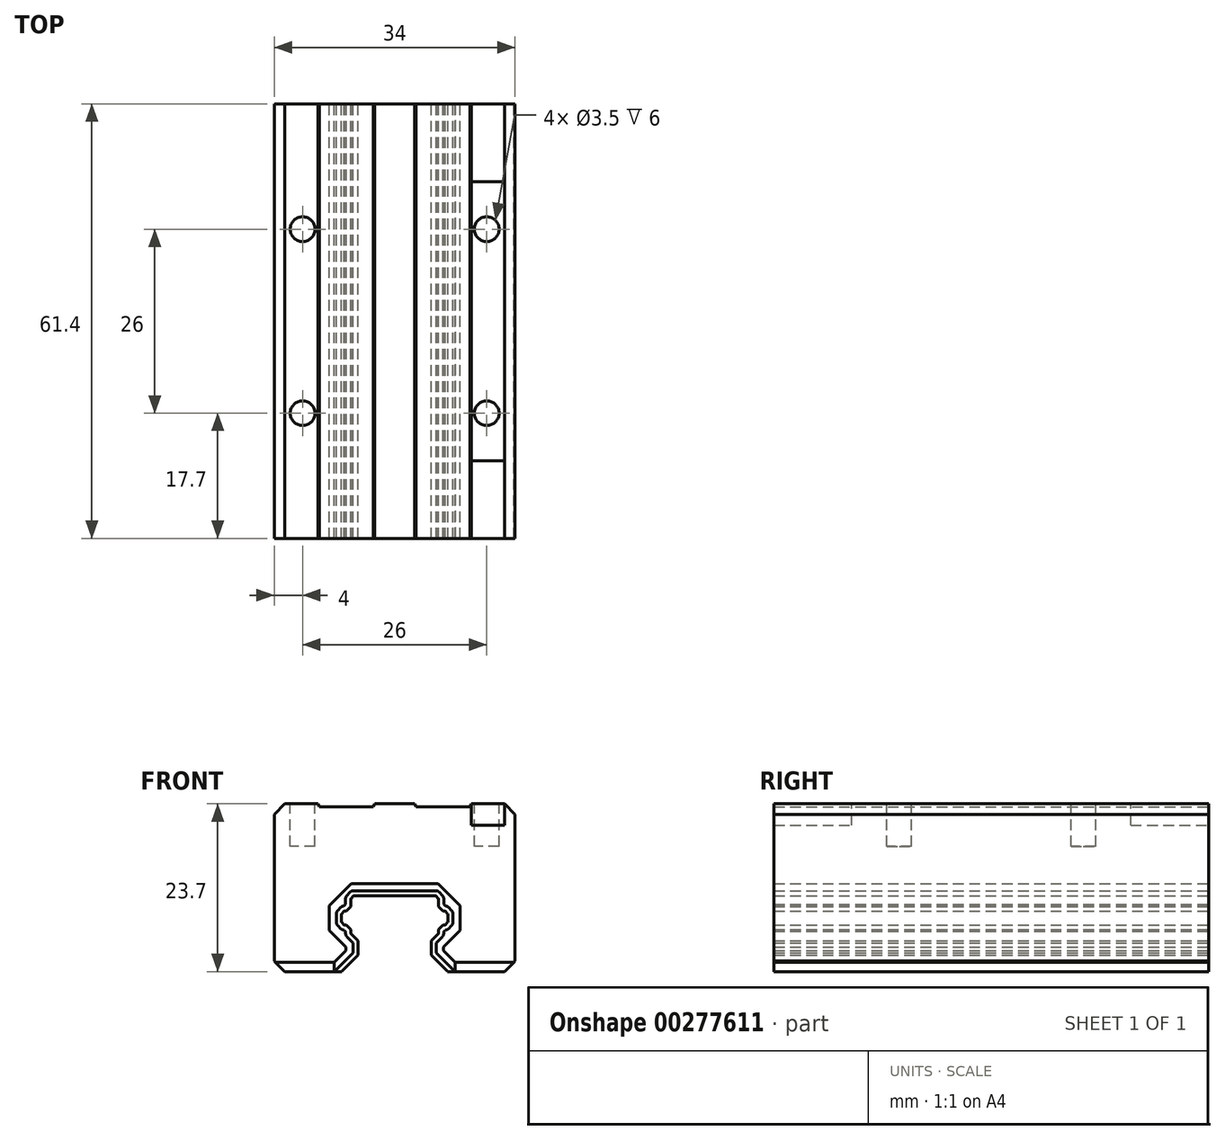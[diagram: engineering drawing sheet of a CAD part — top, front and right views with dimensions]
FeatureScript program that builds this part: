
annotation { "Feature Type Name" : "Feature", "Feature Type Description" : "" }
export const myFeature = defineFeature(function(context is Context, id is Id, definition is map)
    precondition{}
    {
        {
            var Q0;
            Q0=qCreatedBy(makeId("Front.planeOp"),FACE);
            var sketch = newSketch(context, id + "F0", { "sketchPlane" : qUnion([Q0])});
            skLineSegment(sketch, "E0", {"start": v(-6.28, -7.5) * mm, "end": v(6.28, -7.5) * mm});
            skLineSegment(sketch, "E1", {"start": v(7.5, -6.28) * mm, "end": v(7.5, -3.22) * mm});
            skLineSegment(sketch, "E2", {"start": v(5.8, 7.5) * mm, "end": v(-5.8, 7.5) * mm});
            skLineSegment(sketch, "E3", {"start": v(-7.5, 4.94) * mm, "end": v(-7.5, 3.79) * mm});
            skLineSegment(sketch, "E4.0", {"start": v(-7.5, -3.2) * mm, "end": v(7.5, -3.2) * mm, "construction": true});
            skLineSegment(sketch, "E5", {"start": v(-7.49, -3.19) * mm, "end": v(-5.15, -0.85) * mm});
            skLineSegment(sketch, "E6", {"start": v(0, 7.5) * mm, "end": v(0, -7.5) * mm, "construction": true});
            skLineSegment(sketch, "E7", {"start": v(-5.15, -0.85) * mm, "end": v(-5.15, 1.15) * mm});
            skLineSegment(sketch, "E8", {"start": v(-5.15, 1.15) * mm, "end": v(-6.2, 2.2) * mm});
            skLineSegment(sketch, "E9", {"start": v(-6.22, 2.23) * mm, "end": v(-6.22, 2.76) * mm});
            skLineSegment(sketch, "E10.0", {"start": v(-7.08, 5.37) * mm, "end": v(-6.82, 5.37) * mm});
            skLineSegment(sketch, "E11", {"start": v(-6.82, 5.37) * mm, "end": v(-6.22, 5.97) * mm});
            skLineSegment(sketch, "E12.MirrorCS", {"start": v(-6.82, 3.37) * mm, "end": v(-6.22, 2.76) * mm});
            skPoint(sketch, "E13.orphan", {"position": v(-6.22, 5.97) * mm});
            skLineSegment(sketch, "E14.trimOffspring", {"start": v(-6.22, 5.97) * mm, "end": v(-6.22, 7.06) * mm});
            skLineSegment(sketch, "E15", {"start": v(-6.82, 3.37) * mm, "end": v(-7.08, 3.37) * mm});
            skLineSegment(sketch, "E16.trimOffspring", {"start": v(-7.5, -3.22) * mm, "end": v(-7.5, -6.28) * mm});
            skPoint(sketch, "E17.orphan", {"position": v(-7.5, 7.5) * mm});
            skLineSegment(sketch, "E18", {"start": v(-6.22, 5.97) * mm, "end": v(-6.22, 2.76) * mm, "construction": true});
            skLineSegment(sketch, "E19", {"start": v(-6.82, 3.37) * mm, "end": v(-6.22, 3.37) * mm, "construction": true});
            skLineSegment(sketch, "E20", {"start": v(-6.82, 5.37) * mm, "end": v(-6.22, 5.37) * mm, "construction": true});
            skLineSegment(sketch, "E21", {"start": v(-7.49, 4.98) * mm, "end": v(-7.11, 5.35) * mm});
            skLineSegment(sketch, "E22.MirrorCS", {"start": v(-7.49, 3.75) * mm, "end": v(-7.11, 3.38) * mm});
            skPoint(sketch, "E23.orphan", {"position": v(-7.5, 5.37) * mm});
            skPoint(sketch, "E24.orphan", {"position": v(-7.5, 3.37) * mm});
            skLineSegment(sketch, "E25.MirrorCS", {"start": v(7.49, -3.19) * mm, "end": v(5.15, -0.85) * mm});
            skLineSegment(sketch, "E26.MirrorCS", {"start": v(5.15, -0.85) * mm, "end": v(5.15, 1.15) * mm});
            skLineSegment(sketch, "E27.MirrorCS", {"start": v(5.15, 1.15) * mm, "end": v(6.2, 2.2) * mm});
            skLineSegment(sketch, "E28.MirrorCS", {"start": v(6.22, 2.23) * mm, "end": v(6.22, 2.76) * mm});
            skLineSegment(sketch, "E29.MirrorCS", {"start": v(6.82, 3.37) * mm, "end": v(6.22, 2.76) * mm});
            skLineSegment(sketch, "E30.MirrorCS", {"start": v(6.82, 3.37) * mm, "end": v(7.08, 3.37) * mm});
            skLineSegment(sketch, "E31.MirrorCS", {"start": v(7.49, 3.75) * mm, "end": v(7.11, 3.38) * mm});
            skLineSegment(sketch, "E32.MirrorCS", {"start": v(7.5, 4.94) * mm, "end": v(7.5, 3.79) * mm});
            skLineSegment(sketch, "E33.MirrorCS", {"start": v(7.49, 4.98) * mm, "end": v(7.11, 5.35) * mm});
            skLineSegment(sketch, "E34.MirrorCS", {"start": v(7.08, 5.37) * mm, "end": v(6.82, 5.37) * mm});
            skLineSegment(sketch, "E35.MirrorCS", {"start": v(6.82, 5.37) * mm, "end": v(6.22, 5.97) * mm});
            skLineSegment(sketch, "E36.MirrorCS", {"start": v(6.22, 5.97) * mm, "end": v(6.22, 7.06) * mm});
            skPoint(sketch, "E37.orphan", {"position": v(7.5, 7.5) * mm});
            skLineSegment(sketch, "E38.trimOffspring", {"start": v(7.5, 3.77) * mm, "end": v(7.5, 4.97) * mm});
            skLineSegment(sketch, "E39", {"start": v(-7.49, -6.31) * mm, "end": v(-6.31, -7.49) * mm});
            skPoint(sketch, "E40.orphan", {"position": v(-7.5, -7.5) * mm});
            skLineSegment(sketch, "E41.MirrorCS", {"start": v(7.49, -6.31) * mm, "end": v(6.31, -7.49) * mm});
            skPoint(sketch, "E42.orphan", {"position": v(7.5, -7.5) * mm});
            skPoint(sketch, "E43", {"position": v(0, 0) * mm});
            skLineSegment(sketch, "E44", {"start": v(6.82, 5.37) * mm, "end": v(-6.82, 5.37) * mm, "construction": true});
            skLineSegment(sketch, "E45", {"start": v(6.82, 3.37) * mm, "end": v(-6.82, 3.37) * mm, "construction": true});
            skPoint(sketch, "E46.start.orphan", {"position": v(-7.5, 4.37) * mm});
            skLineSegment(sketch, "E47", {"start": v(-6.2, 7.1) * mm, "end": v(-5.83, 7.48) * mm});
            skLineSegment(sketch, "E48.MirrorCS", {"start": v(6.2, 7.1) * mm, "end": v(5.83, 7.48) * mm});
            skPoint(sketch, "E49.orphan", {"position": v(-6.22, 7.5) * mm});
            skPoint(sketch, "E50.orphan", {"position": v(6.22, 7.5) * mm});
            skPoint(sketch, "E51.visualSharp", {"position": v(-5.82, 7.5) * mm});
            skArc(sketch, "E51.filletArc", {"start": v(-5.8, 7.5) * mm, "mid": v(-5.81, 7.5) * mm, "end": v(-5.83, 7.48) * mm});
            skPoint(sketch, "E52.visualSharp", {"position": v(-6.22, 7.08) * mm});
            skArc(sketch, "E52.filletArc", {"start": v(-6.2, 7.1) * mm, "mid": v(-6.21, 7.08) * mm, "end": v(-6.22, 7.06) * mm});
            skPoint(sketch, "E53.visualSharp", {"position": v(-7.1, 5.37) * mm});
            skArc(sketch, "E53.filletArc", {"start": v(-7.08, 5.37) * mm, "mid": v(-7.1, 5.36) * mm, "end": v(-7.11, 5.35) * mm});
            skPoint(sketch, "E54.visualSharp", {"position": v(-7.5, 4.97) * mm});
            skArc(sketch, "E54.filletArc", {"start": v(-7.49, 4.98) * mm, "mid": v(-7.5, 4.96) * mm, "end": v(-7.5, 4.94) * mm});
            skPoint(sketch, "E55.visualSharp", {"position": v(-7.5, 3.77) * mm});
            skArc(sketch, "E55.filletArc", {"start": v(-7.5, 3.79) * mm, "mid": v(-7.5, 3.77) * mm, "end": v(-7.49, 3.75) * mm});
            skPoint(sketch, "E56.visualSharp", {"position": v(-7.1, 3.37) * mm});
            skArc(sketch, "E56.filletArc", {"start": v(-7.11, 3.38) * mm, "mid": v(-7.1, 3.37) * mm, "end": v(-7.08, 3.37) * mm});
            skPoint(sketch, "E57.visualSharp", {"position": v(-6.22, 2.2) * mm});
            skArc(sketch, "E57.filletArc", {"start": v(-6.22, 2.23) * mm, "mid": v(-6.21, 2.2) * mm, "end": v(-6.2, 2.2) * mm});
            skPoint(sketch, "E58.visualSharp", {"position": v(-7.5, -3.2) * mm});
            skArc(sketch, "E58.filletArc", {"start": v(-7.49, -3.19) * mm, "mid": v(-7.5, -3.2) * mm, "end": v(-7.5, -3.22) * mm});
            skPoint(sketch, "E59.visualSharp", {"position": v(-7.5, -6.3) * mm});
            skArc(sketch, "E59.filletArc", {"start": v(-7.5, -6.28) * mm, "mid": v(-7.5, -6.3) * mm, "end": v(-7.49, -6.31) * mm});
            skPoint(sketch, "E60.visualSharp", {"position": v(-6.3, -7.5) * mm});
            skArc(sketch, "E60.filletArc", {"start": v(-6.31, -7.49) * mm, "mid": v(-6.3, -7.5) * mm, "end": v(-6.28, -7.5) * mm});
            skPoint(sketch, "E61.visualSharp", {"position": v(6.3, -7.5) * mm});
            skArc(sketch, "E61.filletArc", {"start": v(6.28, -7.5) * mm, "mid": v(6.3, -7.5) * mm, "end": v(6.31, -7.49) * mm});
            skPoint(sketch, "E62.visualSharp", {"position": v(7.5, -6.3) * mm});
            skArc(sketch, "E62.filletArc", {"start": v(7.49, -6.31) * mm, "mid": v(7.5, -6.3) * mm, "end": v(7.5, -6.28) * mm});
            skPoint(sketch, "E63.visualSharp", {"position": v(7.5, -3.2) * mm});
            skArc(sketch, "E63.filletArc", {"start": v(7.5, -3.22) * mm, "mid": v(7.5, -3.2) * mm, "end": v(7.49, -3.19) * mm});
            skPoint(sketch, "E64.visualSharp", {"position": v(6.22, 2.2) * mm});
            skArc(sketch, "E64.filletArc", {"start": v(6.2, 2.2) * mm, "mid": v(6.21, 2.2) * mm, "end": v(6.22, 2.23) * mm});
            skPoint(sketch, "E65.visualSharp", {"position": v(7.1, 3.37) * mm});
            skArc(sketch, "E65.filletArc", {"start": v(7.08, 3.37) * mm, "mid": v(7.1, 3.37) * mm, "end": v(7.11, 3.38) * mm});
            skPoint(sketch, "E66.visualSharp", {"position": v(7.5, 3.77) * mm});
            skArc(sketch, "E66.filletArc", {"start": v(7.49, 3.75) * mm, "mid": v(7.5, 3.77) * mm, "end": v(7.5, 3.79) * mm});
            skPoint(sketch, "E67.visualSharp", {"position": v(7.5, 4.97) * mm});
            skArc(sketch, "E67.filletArc", {"start": v(7.5, 4.94) * mm, "mid": v(7.5, 4.96) * mm, "end": v(7.49, 4.98) * mm});
            skPoint(sketch, "E68.visualSharp", {"position": v(7.1, 5.37) * mm});
            skArc(sketch, "E68.filletArc", {"start": v(7.11, 5.35) * mm, "mid": v(7.1, 5.36) * mm, "end": v(7.08, 5.37) * mm});
            skPoint(sketch, "E69.visualSharp", {"position": v(6.22, 7.08) * mm});
            skArc(sketch, "E69.filletArc", {"start": v(6.22, 7.06) * mm, "mid": v(6.21, 7.08) * mm, "end": v(6.2, 7.1) * mm});
            skPoint(sketch, "E70.visualSharp", {"position": v(5.82, 7.5) * mm});
            skArc(sketch, "E70.filletArc", {"start": v(5.83, 7.48) * mm, "mid": v(5.81, 7.5) * mm, "end": v(5.8, 7.5) * mm});
            skSolve(sketch);
        }
        {
            var Q0;
            Q0=qCreatedBy(makeId("Front.planeOp"),FACE);
            var sketch = newSketch(context, id + "F1", { "sketchPlane" : qUnion([Q0])});
            skLineSegment(sketch, "E71", {"start": v(-7.03, -9.06) * mm, "end": v(7.97, -9.06) * mm});
            skLineSegment(sketch, "E72.0", {"start": v(-7.49, -6.31) * mm, "end": v(-6.31, -7.49) * mm});
            skLineSegment(sketch, "E73.0", {"start": v(-7.5, -3.22) * mm, "end": v(-7.5, -6.28) * mm});
            skLineSegment(sketch, "E74.0", {"start": v(-7.49, -3.19) * mm, "end": v(-5.15, -0.85) * mm});
            skLineSegment(sketch, "E75.0", {"start": v(-5.15, -0.85) * mm, "end": v(-5.15, 1.15) * mm});
            skLineSegment(sketch, "E76.0", {"start": v(-5.15, 1.15) * mm, "end": v(-6.2, 2.2) * mm});
            skLineSegment(sketch, "E77.0", {"start": v(-6.22, 2.23) * mm, "end": v(-6.22, 2.76) * mm});
            skLineSegment(sketch, "E78.0", {"start": v(-6.82, 3.37) * mm, "end": v(-6.22, 2.76) * mm});
            skLineSegment(sketch, "E79.0", {"start": v(-6.82, 3.37) * mm, "end": v(-7.08, 3.37) * mm});
            skArc(sketch, "E80.0", {"start": v(-7.11, 3.38) * mm, "mid": v(-7.1, 3.37) * mm, "end": v(-7.08, 3.37) * mm});
            skLineSegment(sketch, "E81.0", {"start": v(-7.49, 3.75) * mm, "end": v(-7.11, 3.38) * mm});
            skArc(sketch, "E82.0", {"start": v(-6.22, 2.23) * mm, "mid": v(-6.21, 2.2) * mm, "end": v(-6.2, 2.2) * mm});
            skArc(sketch, "E83.0", {"start": v(-7.49, -3.19) * mm, "mid": v(-7.5, -3.2) * mm, "end": v(-7.5, -3.22) * mm});
            skArc(sketch, "E84.0", {"start": v(-7.5, -6.28) * mm, "mid": v(-7.5, -6.3) * mm, "end": v(-7.49, -6.31) * mm});
            skArc(sketch, "E85.0", {"start": v(-6.31, -7.49) * mm, "mid": v(-6.3, -7.5) * mm, "end": v(-6.28, -7.5) * mm});
            skLineSegment(sketch, "E86.0", {"start": v(-6.28, -7.5) * mm, "end": v(6.28, -7.5) * mm});
            skArc(sketch, "E87.0", {"start": v(6.28, -7.5) * mm, "mid": v(6.3, -7.5) * mm, "end": v(6.31, -7.49) * mm});
            skLineSegment(sketch, "E88.0", {"start": v(7.49, -6.31) * mm, "end": v(6.31, -7.49) * mm});
            skArc(sketch, "E89.0", {"start": v(7.49, -6.31) * mm, "mid": v(7.5, -6.3) * mm, "end": v(7.5, -6.28) * mm});
            skLineSegment(sketch, "E90.0", {"start": v(7.5, -6.28) * mm, "end": v(7.5, -3.22) * mm});
            skArc(sketch, "E91.0", {"start": v(7.5, -3.22) * mm, "mid": v(7.5, -3.2) * mm, "end": v(7.49, -3.19) * mm});
            skLineSegment(sketch, "E92.0", {"start": v(7.49, -3.19) * mm, "end": v(5.15, -0.85) * mm});
            skLineSegment(sketch, "E93.0", {"start": v(5.15, -0.85) * mm, "end": v(5.15, 1.15) * mm});
            skLineSegment(sketch, "E94.0", {"start": v(5.15, 1.15) * mm, "end": v(6.2, 2.2) * mm});
            skArc(sketch, "E95.0", {"start": v(6.2, 2.2) * mm, "mid": v(6.21, 2.2) * mm, "end": v(6.22, 2.23) * mm});
            skLineSegment(sketch, "E96.0", {"start": v(6.22, 2.23) * mm, "end": v(6.22, 2.76) * mm});
            skLineSegment(sketch, "E97.0", {"start": v(6.82, 3.37) * mm, "end": v(6.22, 2.76) * mm});
            skLineSegment(sketch, "E98.0", {"start": v(6.82, 3.37) * mm, "end": v(7.08, 3.37) * mm});
            skArc(sketch, "E99.0", {"start": v(7.08, 3.37) * mm, "mid": v(7.1, 3.37) * mm, "end": v(7.11, 3.38) * mm});
            skLineSegment(sketch, "E100.0", {"start": v(7.49, 3.75) * mm, "end": v(7.11, 3.38) * mm});
            skArc(sketch, "E101.0", {"start": v(7.49, 3.75) * mm, "mid": v(7.5, 3.77) * mm, "end": v(7.5, 3.79) * mm});
            skLineSegment(sketch, "E102.0", {"start": v(7.5, 3.79) * mm, "end": v(7.5, 4.94) * mm});
            skArc(sketch, "E103.0", {"start": v(7.5, 4.94) * mm, "mid": v(7.5, 4.96) * mm, "end": v(7.49, 4.98) * mm});
            skLineSegment(sketch, "E104.0", {"start": v(7.49, 4.98) * mm, "end": v(7.11, 5.35) * mm});
            skArc(sketch, "E105.0", {"start": v(7.11, 5.35) * mm, "mid": v(7.1, 5.36) * mm, "end": v(7.08, 5.37) * mm});
            skLineSegment(sketch, "E106.0", {"start": v(7.08, 5.37) * mm, "end": v(6.82, 5.37) * mm});
            skLineSegment(sketch, "E107.0", {"start": v(6.82, 5.37) * mm, "end": v(6.22, 5.97) * mm});
            skLineSegment(sketch, "E108.0", {"start": v(6.22, 5.97) * mm, "end": v(6.22, 7.06) * mm});
            skArc(sketch, "E109.0", {"start": v(6.22, 7.06) * mm, "mid": v(6.21, 7.08) * mm, "end": v(6.2, 7.1) * mm});
            skLineSegment(sketch, "E110.0", {"start": v(6.2, 7.1) * mm, "end": v(5.83, 7.48) * mm});
            skArc(sketch, "E111.0", {"start": v(5.83, 7.48) * mm, "mid": v(5.81, 7.5) * mm, "end": v(5.8, 7.5) * mm});
            skLineSegment(sketch, "E112.0", {"start": v(5.8, 7.5) * mm, "end": v(-5.8, 7.5) * mm});
            skArc(sketch, "E113.0", {"start": v(-5.8, 7.5) * mm, "mid": v(-5.81, 7.5) * mm, "end": v(-5.83, 7.48) * mm});
            skLineSegment(sketch, "E114.0", {"start": v(-6.2, 7.1) * mm, "end": v(-5.83, 7.48) * mm});
            skArc(sketch, "E115.0", {"start": v(-6.2, 7.1) * mm, "mid": v(-6.21, 7.08) * mm, "end": v(-6.22, 7.06) * mm});
            skLineSegment(sketch, "E116.0", {"start": v(-6.22, 5.97) * mm, "end": v(-6.22, 7.06) * mm});
            skLineSegment(sketch, "E117.0", {"start": v(-6.82, 5.37) * mm, "end": v(-6.22, 5.97) * mm});
            skPoint(sketch, "E118.0", {"position": v(-6.95, 5.37) * mm});
            skLineSegment(sketch, "E119.0", {"start": v(-7.08, 5.37) * mm, "end": v(-6.82, 5.37) * mm});
            skPoint(sketch, "E120.0", {"position": v(-7.1, 5.36) * mm});
            skArc(sketch, "E121.0", {"start": v(-7.08, 5.37) * mm, "mid": v(-7.1, 5.36) * mm, "end": v(-7.11, 5.35) * mm});
            skLineSegment(sketch, "E122.0", {"start": v(-7.49, 4.98) * mm, "end": v(-7.11, 5.35) * mm});
            skArc(sketch, "E123.0", {"start": v(-7.49, 4.98) * mm, "mid": v(-7.5, 4.96) * mm, "end": v(-7.5, 4.94) * mm});
            skLineSegment(sketch, "E124.0", {"start": v(-7.5, 4.94) * mm, "end": v(-7.5, 3.79) * mm});
            skArc(sketch, "E125.0", {"start": v(-7.5, 3.79) * mm, "mid": v(-7.5, 3.77) * mm, "end": v(-7.49, 3.75) * mm});
            skPoint(sketch, "E126.orphan", {"position": v(7.5, 4.97) * mm});
            skPoint(sketch, "E127.orphan", {"position": v(7.5, 3.77) * mm});
            skLineSegment(sketch, "E128.2", {"start": v(-8.52, -3.2) * mm, "end": v(-5.87, -0.56) * mm});
            skLineSegment(sketch, "E128.3", {"start": v(-5.87, -0.56) * mm, "end": v(-5.87, 0.85) * mm});
            skLineSegment(sketch, "E128.4", {"start": v(-5.87, 0.85) * mm, "end": v(-6.7, 1.68) * mm});
            skArc(sketch, "E128.5", {"start": v(-6.94, 2.23) * mm, "mid": v(-6.88, 1.93) * mm, "end": v(-6.7, 1.68) * mm});
            skLineSegment(sketch, "E128.6", {"start": v(-6.94, 2.23) * mm, "end": v(-6.94, 2.46) * mm});
            skLineSegment(sketch, "E128.7", {"start": v(-7.12, 2.65) * mm, "end": v(-6.94, 2.46) * mm});
            skArc(sketch, "E128.8", {"start": v(-7.62, 2.87) * mm, "mid": v(-7.4, 2.71) * mm, "end": v(-7.12, 2.65) * mm});
            skLineSegment(sketch, "E128.9", {"start": v(-8, 3.24) * mm, "end": v(-7.62, 2.87) * mm});
            skArc(sketch, "E128.10", {"start": v(-8.22, 3.79) * mm, "mid": v(-8.16, 3.5) * mm, "end": v(-8, 3.24) * mm});
            skLineSegment(sketch, "E128.11", {"start": v(-8.22, 4.94) * mm, "end": v(-8.22, 3.79) * mm});
            skArc(sketch, "E128.12", {"start": v(-8, 5.49) * mm, "mid": v(-8.16, 5.24) * mm, "end": v(-8.22, 4.94) * mm});
            skLineSegment(sketch, "E128.13", {"start": v(-8, 5.49) * mm, "end": v(-7.62, 5.86) * mm});
            skArc(sketch, "E128.14", {"start": v(-7.12, 6.08) * mm, "mid": v(-7.4, 6.02) * mm, "end": v(-7.62, 5.86) * mm});
            skLineSegment(sketch, "E128.15", {"start": v(-7.12, 6.08) * mm, "end": v(-6.94, 6.27) * mm});
            skLineSegment(sketch, "E128.16", {"start": v(-6.94, 6.27) * mm, "end": v(-6.94, 7.06) * mm});
            skArc(sketch, "E128.17", {"start": v(-6.72, 7.59) * mm, "mid": v(-6.88, 7.34) * mm, "end": v(-6.94, 7.06) * mm});
            skLineSegment(sketch, "E128.18", {"start": v(-6.72, 7.59) * mm, "end": v(-6.35, 7.98) * mm});
            skLineSegment(sketch, "E128.19", {"start": v(8, 3.24) * mm, "end": v(7.62, 2.87) * mm});
            skArc(sketch, "E128.20", {"start": v(7.12, 2.65) * mm, "mid": v(7.4, 2.71) * mm, "end": v(7.62, 2.87) * mm});
            skLineSegment(sketch, "E128.21", {"start": v(7.12, 2.65) * mm, "end": v(6.94, 2.46) * mm});
            skLineSegment(sketch, "E128.22", {"start": v(6.94, 2.23) * mm, "end": v(6.94, 2.46) * mm});
            skArc(sketch, "E128.23", {"start": v(6.7, 1.68) * mm, "mid": v(6.88, 1.93) * mm, "end": v(6.94, 2.23) * mm});
            skLineSegment(sketch, "E128.24", {"start": v(5.87, 0.85) * mm, "end": v(6.7, 1.68) * mm});
            skLineSegment(sketch, "E128.27", {"start": v(8.52, -3.2) * mm, "end": v(5.87, -0.56) * mm});
            skLineSegment(sketch, "E128.28", {"start": v(5.87, -0.56) * mm, "end": v(5.87, 0.85) * mm});
            skArc(sketch, "E128.29", {"start": v(8, 3.24) * mm, "mid": v(8.16, 3.5) * mm, "end": v(8.22, 3.79) * mm});
            skLineSegment(sketch, "E128.30", {"start": v(8.22, 3.79) * mm, "end": v(8.22, 4.94) * mm});
            skArc(sketch, "E128.31", {"start": v(8.22, 4.94) * mm, "mid": v(8.16, 5.24) * mm, "end": v(8, 5.49) * mm});
            skLineSegment(sketch, "E128.32", {"start": v(8, 5.49) * mm, "end": v(7.62, 5.86) * mm});
            skArc(sketch, "E128.33", {"start": v(7.62, 5.86) * mm, "mid": v(7.4, 6.02) * mm, "end": v(7.12, 6.08) * mm});
            skLineSegment(sketch, "E128.34", {"start": v(7.12, 6.08) * mm, "end": v(6.94, 6.27) * mm});
            skLineSegment(sketch, "E128.35", {"start": v(6.94, 6.27) * mm, "end": v(6.94, 7.06) * mm});
            skArc(sketch, "E128.36", {"start": v(6.94, 7.06) * mm, "mid": v(6.88, 7.34) * mm, "end": v(6.72, 7.59) * mm});
            skLineSegment(sketch, "E128.37", {"start": v(6.72, 7.59) * mm, "end": v(6.35, 7.98) * mm});
            skArc(sketch, "E128.38", {"start": v(6.35, 7.98) * mm, "mid": v(6.1, 8.16) * mm, "end": v(5.8, 8.22) * mm});
            skLineSegment(sketch, "E128.39", {"start": v(5.8, 8.22) * mm, "end": v(-5.8, 8.22) * mm});
            skArc(sketch, "E128.40", {"start": v(-5.8, 8.22) * mm, "mid": v(-6.1, 8.16) * mm, "end": v(-6.35, 7.98) * mm});
            skLineSegment(sketch, "E129", {"start": v(6.28, -7.5) * mm, "end": v(-6.28, -7.5) * mm, "construction": true});
            skPoint(sketch, "E130.endSnap0", {"position": v(8.22, -4.75) * mm});
            skLineSegment(sketch, "E131", {"start": v(-15.5, 20.5) * mm, "end": v(-10.8, 20.5) * mm});
            skLineSegment(sketch, "E132.0", {"start": v(-6.87, -0.22) * mm, "end": v(-6.87, 0.26) * mm});
            skLineSegment(sketch, "E133.0", {"start": v(-9.22, 6.12) * mm, "end": v(-9.22, 2.6) * mm});
            skPoint(sketch, "E134.endSnap0", {"position": v(-9.22, 4.37) * mm});
            skPoint(sketch, "E135.orphan", {"position": v(-9.22, 4.94) * mm});
            skPoint(sketch, "E136.orphan", {"position": v(-9.22, 3.79) * mm});
            skLineSegment(sketch, "E137", {"start": v(-9.22, 6.12) * mm, "end": v(-6.12, 9.22) * mm});
            skLineSegment(sketch, "E138", {"start": v(-9.22, 2.6) * mm, "end": v(-6.87, 0.26) * mm});
            skLineSegment(sketch, "E139", {"start": v(-6.87, -0.22) * mm, "end": v(-8.52, -1.86) * mm});
            skLineSegment(sketch, "E140", {"start": v(-6.87, 0) * mm, "end": v(-8.75, 0) * mm, "construction": true});
            skLineSegment(sketch, "E141", {"start": v(-15.5, -3.2) * mm, "end": v(-7.5, -3.2) * mm});
            skLineSegment(sketch, "E142", {"start": v(0, -7.5) * mm, "end": v(0, -7.5) * mm});
            skPoint(sketch, "E142.endSnap0", {"position": v(0, -7.5) * mm});
            skLineSegment(sketch, "E143.MirrorCS", {"start": v(9.22, 6.12) * mm, "end": v(6.12, 9.22) * mm});
            skLineSegment(sketch, "E144.MirrorCS", {"start": v(9.22, 6.12) * mm, "end": v(9.22, 2.6) * mm});
            skLineSegment(sketch, "E145.MirrorCS", {"start": v(9.22, 2.6) * mm, "end": v(6.87, 0.26) * mm});
            skLineSegment(sketch, "E146.MirrorCS", {"start": v(6.87, -0.22) * mm, "end": v(6.87, 0.26) * mm});
            skLineSegment(sketch, "E147.MirrorCS", {"start": v(6.87, -0.22) * mm, "end": v(8.52, -1.86) * mm});
            skLineSegment(sketch, "E148", {"start": v(-8.52, -3.2) * mm, "end": v(-8.52, -1.86) * mm});
            skLineSegment(sketch, "E149.MirrorCS", {"start": v(8.52, -3.2) * mm, "end": v(8.52, -1.86) * mm});
            skLineSegment(sketch, "E150", {"start": v(-6.12, 9.22) * mm, "end": v(6.12, 9.22) * mm});
            skLineSegment(sketch, "E151", {"start": v(15.5, -3.2) * mm, "end": v(7.5, -3.2) * mm});
            skPoint(sketch, "E151.endSnap0", {"position": v(7.5, -3.2) * mm});
            skLineSegment(sketch, "E152", {"start": v(-17, -1.7) * mm, "end": v(-15.5, -3.2) * mm});
            skLineSegment(sketch, "E153", {"start": v(15.5, 20.5) * mm, "end": v(17, 19) * mm});
            skLineSegment(sketch, "E154", {"start": v(-7.5, -4.05) * mm, "end": v(7.5, -4.05) * mm, "construction": true});
            skLineSegment(sketch, "E155", {"start": v(0, -4.05) * mm, "end": v(0, 23.56) * mm, "construction": true});
            skLineSegment(sketch, "E156.MirrorCS", {"start": v(-15.5, 20.5) * mm, "end": v(-17, 19) * mm});
            skLineSegment(sketch, "E157.MirrorCS", {"start": v(17, -1.7) * mm, "end": v(15.5, -3.2) * mm});
            skLineSegment(sketch, "E158.trimOffspring", {"start": v(17, -1.7) * mm, "end": v(17, 19) * mm});
            skPoint(sketch, "E159.orphan", {"position": v(17, -4.75) * mm});
            skPoint(sketch, "E160.orphan", {"position": v(17, -7.5) * mm});
            skPoint(sketch, "E130.start.orphan", {"position": v(7.5, -4.75) * mm});
            skPoint(sketch, "E161.orphan", {"position": v(-17, -3.2) * mm});
            skLineSegment(sketch, "E162.trimOffspring", {"start": v(-17, -1.7) * mm, "end": v(-17, 19) * mm});
            skPoint(sketch, "E163.start.orphan", {"position": v(-7.5, -4.75) * mm});
            skPoint(sketch, "E164.end.orphan", {"position": v(-17, -7.5) * mm});
            skLineSegment(sketch, "E165", {"start": v(-10.8, 20.5) * mm, "end": v(-10.65, 20.1) * mm});
            skLineSegment(sketch, "E166.trimOffspring", {"start": v(-10.65, 20.1) * mm, "end": v(-3, 20.1) * mm});
            skLineSegment(sketch, "E167", {"start": v(-3, 20.1) * mm, "end": v(-2.85, 20.5) * mm});
            skLineSegment(sketch, "E168.MirrorCS", {"start": v(10.8, 20.5) * mm, "end": v(10.65, 20.1) * mm});
            skLineSegment(sketch, "E169.MirrorCS", {"start": v(3, 20.1) * mm, "end": v(2.85, 20.5) * mm});
            skLineSegment(sketch, "E170.trimOffspring", {"start": v(-2.85, 20.5) * mm, "end": v(2.85, 20.5) * mm});
            skLineSegment(sketch, "E171.trimOffspring", {"start": v(10.8, 20.5) * mm, "end": v(15.5, 20.5) * mm});
            skLineSegment(sketch, "E172.trimOffspring", {"start": v(3, 20.1) * mm, "end": v(10.65, 20.1) * mm});
            skPoint(sketch, "E173.start.orphan", {"position": v(17, 20.5) * mm});
            skArc(sketch, "E174", {"start": v(-7.49, -3.19) * mm, "mid": v(-7.5, -3.2) * mm, "end": v(-7.5, -3.2) * mm});
            skLineSegment(sketch, "E175", {"start": v(-6.22, 2.76) * mm, "end": v(-6.82, 3.37) * mm});
            skLineSegment(sketch, "E176", {"start": v(-7.11, 3.38) * mm, "end": v(-7.49, 3.75) * mm});
            skLineSegment(sketch, "E177", {"start": v(-7.5, 3.79) * mm, "end": v(-7.5, 4.94) * mm});
            skLineSegment(sketch, "E178", {"start": v(-5.8, 7.5) * mm, "end": v(5.8, 7.5) * mm});
            skLineSegment(sketch, "E179", {"start": v(5.83, 7.48) * mm, "end": v(6.2, 7.1) * mm});
            skLineSegment(sketch, "E180", {"start": v(6.22, 7.06) * mm, "end": v(6.22, 5.97) * mm});
            skLineSegment(sketch, "E181", {"start": v(6.22, 5.97) * mm, "end": v(6.82, 5.37) * mm});
            skLineSegment(sketch, "E182", {"start": v(6.82, 5.37) * mm, "end": v(7.08, 5.37) * mm});
            skLineSegment(sketch, "E183", {"start": v(7.11, 5.35) * mm, "end": v(7.49, 4.98) * mm});
            skLineSegment(sketch, "E184", {"start": v(7.5, 4.94) * mm, "end": v(7.5, 3.79) * mm});
            skLineSegment(sketch, "E185", {"start": v(7.08, 3.37) * mm, "end": v(6.82, 3.37) * mm});
            skLineSegment(sketch, "E186", {"start": v(6.22, 2.76) * mm, "end": v(6.22, 2.23) * mm});
            skLineSegment(sketch, "E187", {"start": v(6.2, 2.2) * mm, "end": v(5.15, 1.15) * mm});
            skLineSegment(sketch, "E188", {"start": v(5.15, 1.15) * mm, "end": v(5.15, -0.85) * mm});
            skLineSegment(sketch, "E189", {"start": v(5.15, -0.85) * mm, "end": v(7.49, -3.19) * mm});
            skLineSegment(sketch, "E190.0", {"start": v(-15.5, 1.8) * mm, "end": v(-7.5, 1.8) * mm, "construction": true});
            skLineSegment(sketch, "E191", {"start": v(-8.52, -1.86) * mm, "end": v(-16.84, -1.86) * mm});
            skLineSegment(sketch, "E192", {"start": v(8.52, -1.86) * mm, "end": v(16.84, -1.86) * mm});
            skSolve(sketch);
        }
        {
            var Q0;
            Q0=makeQuery(id+"F1.imprint","IMPRINT",FACE,{"disambiguationData":[TD([[makeQuery(id+"F1.imprint","IMPRINT",EDGE,{"derivedFrom":sQuery(id+"F1.wireOp",EDGE,"E131")}),-1.0]])]});
            extrude(context, id + "F2", {"entities" : qUnion([Q0]), "endBound" : BoundingType.SYMMETRIC, "depth" : 61.4 * mm});
        }
        {
            var Q0;
            Q0=makeQuery(id+"F1.imprint","IMPRINT",FACE,{"disambiguationData":[TD([[makeQuery(id+"F1.imprint","IMPRINT",EDGE,{"derivedFrom":sQuery(id+"F1.wireOp",EDGE,"E128.2")}),1.0]])]});
            extrude(context, id + "F3", {"entities" : qUnion([Q0]), "endBound" : BoundingType.SYMMETRIC, "depth" : 61.4 * mm});
        }
        {
            var Q0;
            {var subQ6=sQuery(id+"F1.wireOp",EDGE,"E128.2");Q0=makeQuery(id+"F1.imprint","IMPRINT",FACE,{"disambiguationData":[TD([[makeQuery(id+"F1.imprint","IMPRINT",EDGE,{"derivedFrom":subQ6}),-1.0]])]});}
            extrude(context, id + "F4", {"entities" : qUnion([Q0]), "endBound" : BoundingType.SYMMETRIC, "depth" : 61.4 * mm});
        }
        {
            var Q0;
            {var subQ0=sQuery(id+"F1.wireOp",EDGE,"E148");Q0=makeQuery(id+"F1.imprint","IMPRINT",FACE,{"disambiguationData":[TD([[makeQuery(id+"F1.imprint","IMPRINT",EDGE,{"derivedFrom":subQ0}),1.0]])]});}
            var Q1;
            {var subQ0=sQuery(id+"F1.wireOp",EDGE,"E149.MirrorCS");Q1=makeQuery(id+"F1.imprint","IMPRINT",FACE,{"disambiguationData":[TD([[makeQuery(id+"F1.imprint","IMPRINT",EDGE,{"derivedFrom":subQ0}),-1.0]])]});}
            extrude(context, id + "F5", {"entities" : qUnion([Q0, Q1]), "endBound" : BoundingType.SYMMETRIC, "depth" : 61.4 * mm});
        }
        {
            var Q0;
            Q0=makeQuery(id+"F2.opExtrude","SWEPT_FACE",FACE,{"disambiguationData":[OSD([sQuery(id+"F1.wireOp",EDGE,"E171.trimOffspring")])]});
            var sketch = newSketch(context, id + "F6", { "sketchPlane" : qUnion([Q0])});
            skLineSegment(sketch, "E193.0.1", {"start": v(17, 30.7) * mm, "end": v(17, -30.7) * mm});
            skLineSegment(sketch, "E193.0.3", {"start": v(17, -30.7) * mm, "end": v(17, 30.7) * mm});
            skLineSegment(sketch, "E194.0.1", {"start": v(-17, 30.7) * mm, "end": v(-17, -30.7) * mm});
            skLineSegment(sketch, "E194.0.3", {"start": v(-17, -30.7) * mm, "end": v(-17, 30.7) * mm});
            skLineSegment(sketch, "E195", {"start": v(17, 30.7) * mm, "end": v(-17, 30.7) * mm});
            skLineSegment(sketch, "E196", {"start": v(-17, -30.7) * mm, "end": v(17, -30.7) * mm});
            skLineSegment(sketch, "E197.0", {"start": v(17, 19.7) * mm, "end": v(-17, 19.7) * mm});
            skLineSegment(sketch, "E198.0", {"start": v(-17, -19.7) * mm, "end": v(17, -19.7) * mm});
            skLineSegment(sketch, "E199.0", {"start": v(13, -30.7) * mm, "end": v(13, 30.7) * mm, "construction": true});
            skLineSegment(sketch, "E200.0", {"start": v(-13, -30.7) * mm, "end": v(-13, 30.7) * mm, "construction": true});
            skLineSegment(sketch, "E201", {"start": v(17, 0) * mm, "end": v(-19.88, 0) * mm, "construction": true});
            skPoint(sketch, "E201.endSnap0", {"position": v(17, 0) * mm});
            skLineSegment(sketch, "E202.0", {"start": v(17, 13) * mm, "end": v(-19.88, 13) * mm, "construction": true});
            skLineSegment(sketch, "E203.0", {"start": v(17, -13) * mm, "end": v(-19.88, -13) * mm, "construction": true});
            skCircle(sketch, "E204", {"center": v(13, -13) * mm, "radius": 1.75 * mm});
            skCircle(sketch, "E205", {"center": v(-13, -13) * mm, "radius": 1.75 * mm});
            skCircle(sketch, "E206", {"center": v(13, 13) * mm, "radius": 1.75 * mm});
            skCircle(sketch, "E207", {"center": v(-13, 13) * mm, "radius": 1.75 * mm});
            skSolve(sketch);
        }
        {
            var Q0;
            {var subQ0=sQuery(id+"F6.wireOp",EDGE,"E196");var subQ1=sQuery(id+"F6.wireOp",EDGE,"E193.0.3");var subQ2=makeQuery(id+"F6.imprint","INTERSECT",VERTEX,{"derivedFrom":[subQ1,subQ0]});Q0=makeQuery(id+"F6.imprint","IMPRINT",FACE,{"disambiguationData":[TD([[makeQuery(id+"F6.imprint","IMPRINT",EDGE,{"disambiguationData":[TD([[subQ2,-1.0]])],"derivedFrom":subQ1}),1.0]])]});}
            var Q1;
            {var subQ0=sQuery(id+"F6.wireOp",EDGE,"E196");var subQ1=sQuery(id+"F1.wireOp",EDGE,"E171.trimOffspring");var subQ2=makeQuery(id+"F2.opExtrude","SWEPT_EDGE",EDGE,{"disambiguationData":[OSD([sQuery(id+"F1.wireOp",EDGE,"E153"),subQ1])]});var subQ3=makeQuery(id+"F6.imprint","INTERSECT",VERTEX,{"derivedFrom":[subQ2,subQ0]});Q1=makeQuery(id+"F6.imprint","IMPRINT",FACE,{"disambiguationData":[TD([[makeQuery(id+"F6.imprint","IMPRINT",EDGE,{"disambiguationData":[TD([[subQ3,1.0]])],"derivedFrom":subQ0}),1.0]])]});}
            var Q2;
            {var subQ0=sQuery(id+"F6.wireOp",EDGE,"E196");var subQ1=sQuery(id+"F6.wireOp",EDGE,"E194.0.3");var subQ2=makeQuery(id+"F6.imprint","INTERSECT",VERTEX,{"derivedFrom":[subQ1,subQ0]});Q2=makeQuery(id+"F6.imprint","IMPRINT",FACE,{"disambiguationData":[TD([[makeQuery(id+"F6.imprint","IMPRINT",EDGE,{"disambiguationData":[TD([[subQ2,-1.0]])],"derivedFrom":subQ1}),-1.0]])]});}
            var Q3;
            {var subQ0=sQuery(id+"F6.wireOp",EDGE,"E195");var subQ1=sQuery(id+"F6.wireOp",EDGE,"E194.0.3");var subQ2=makeQuery(id+"F6.imprint","INTERSECT",VERTEX,{"derivedFrom":[subQ1,subQ0]});Q3=makeQuery(id+"F6.imprint","IMPRINT",FACE,{"disambiguationData":[TD([[makeQuery(id+"F6.imprint","IMPRINT",EDGE,{"disambiguationData":[TD([[subQ2,1.0]])],"derivedFrom":subQ1}),-1.0]])]});}
            var Q4;
            {var subQ0=sQuery(id+"F6.wireOp",EDGE,"E195");var subQ1=sQuery(id+"F1.wireOp",EDGE,"E171.trimOffspring");var subQ2=makeQuery(id+"F2.opExtrude","SWEPT_EDGE",EDGE,{"disambiguationData":[OSD([sQuery(id+"F1.wireOp",EDGE,"E153"),subQ1])]});var subQ3=makeQuery(id+"F6.imprint","INTERSECT",VERTEX,{"derivedFrom":[subQ2,subQ0]});var subQ4=makeQuery(id+"F2.opExtrude","SWEPT_EDGE",EDGE,{"disambiguationData":[OSD([sQuery(id+"F1.wireOp",EDGE,"E168.MirrorCS"),subQ1])]});var subQ5=makeQuery(id+"F6.imprint","INTERSECT",VERTEX,{"derivedFrom":[subQ4,subQ0]});Q4=makeQuery(id+"F6.imprint","IMPRINT",FACE,{"disambiguationData":[TD([[makeQuery(id+"F6.imprint","IMPRINT",EDGE,{"disambiguationData":[TD([[subQ3,1.0],[subQ5,-1.0]])],"derivedFrom":subQ0}),-1.0]])]});}
            var Q5;
            {var subQ0=sQuery(id+"F6.wireOp",EDGE,"E195");var subQ1=sQuery(id+"F6.wireOp",EDGE,"E193.0.3");var subQ2=makeQuery(id+"F6.imprint","INTERSECT",VERTEX,{"derivedFrom":[subQ1,subQ0]});Q5=makeQuery(id+"F6.imprint","IMPRINT",FACE,{"disambiguationData":[TD([[makeQuery(id+"F6.imprint","IMPRINT",EDGE,{"disambiguationData":[TD([[subQ2,1.0]])],"derivedFrom":subQ1}),1.0]])]});}
            extrude(context, id + "F7", {"entities" : qUnion([Q0, Q1, Q2, Q3, Q4, Q5]), "operationType" : NewBodyOperationType.REMOVE, "oppositeDirection" : true, "depth" : 3 * mm});
        }
        {
            var Q0;
            Q0=makeQuery(id+"F6.imprint","IMPRINT",FACE,{"disambiguationData":[TD([[makeQuery(id+"F6.imprint","IMPRINT",EDGE,{"derivedFrom":sQuery(id+"F6.wireOp",EDGE,"E206")}),1.0]])]});
            var Q1;
            Q1=makeQuery(id+"F6.imprint","IMPRINT",FACE,{"disambiguationData":[TD([[makeQuery(id+"F6.imprint","IMPRINT",EDGE,{"derivedFrom":sQuery(id+"F6.wireOp",EDGE,"E204")}),1.0]])]});
            var Q2;
            Q2=makeQuery(id+"F6.imprint","IMPRINT",FACE,{"disambiguationData":[TD([[makeQuery(id+"F6.imprint","IMPRINT",EDGE,{"derivedFrom":sQuery(id+"F6.wireOp",EDGE,"E205")}),1.0]])]});
            var Q3;
            Q3=makeQuery(id+"F6.imprint","IMPRINT",FACE,{"disambiguationData":[TD([[makeQuery(id+"F6.imprint","IMPRINT",EDGE,{"derivedFrom":sQuery(id+"F6.wireOp",EDGE,"E207")}),1.0]])]});
            extrude(context, id + "F8", {"entities" : qUnion([Q0, Q1, Q2, Q3]), "operationType" : NewBodyOperationType.REMOVE, "oppositeDirection" : true, "depth" : 6 * mm});
        }
    });
